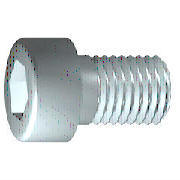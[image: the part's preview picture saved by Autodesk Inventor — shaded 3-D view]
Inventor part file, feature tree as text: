
AUTODESK INVENTOR PART (.ipt)
format: ipt  version: 2023.3 (Build 273359000, 359)  size: 186,368 bytes
history: native  units: mm (DEFAULTED — no unit token found)
features: sketch x2, other x1, extrude x1, plane x1, fillet x1
ambient origin geometry x7: Origin, YZ Plane, XY Plane, X Axis, Y Axis, Z Axis, Center Point
bodies: Solid1 (feature_tree)
feature tree (6):
  other  "Körper"
  extrude  "Loch"  Depth=2.0mm
  plane  "Work Plane1"
  fillet  "Fillet2"  Radius=2.0mm
  sketch  "Skizze1"  dims[d1=19.0mm d2=0.24548mm d3=2.0mm]
  sketch  "Skizze2"  dims[d4=1.0mm d5=60.0deg d6=2.0mm d7=2.0mm d8=1.732051mm d9=3.8mm d10=90.0deg d11=10.0mm d12=0.0mm d13=19.0mm d14=0.0mm d15=0.24538mm d16=0.24538mm d17=0.2mm d19=0.0mm d26=20.0mm d27=45.0deg d28=0.0mm d29=0.0mm d30=0.1mm]
